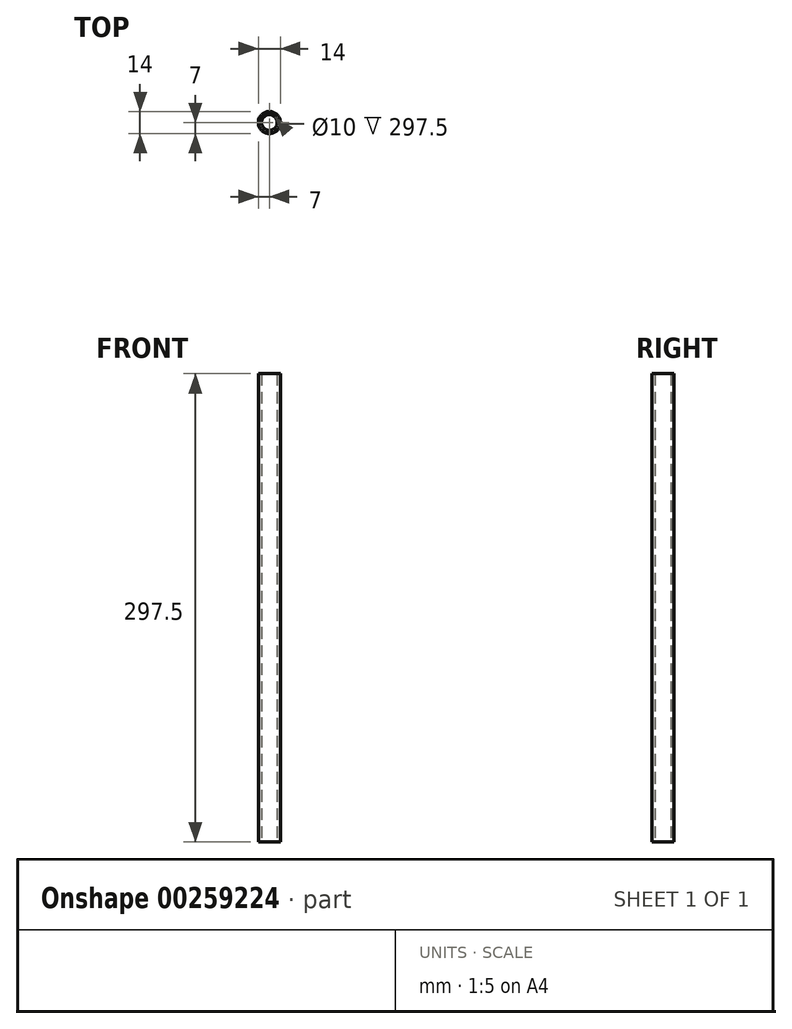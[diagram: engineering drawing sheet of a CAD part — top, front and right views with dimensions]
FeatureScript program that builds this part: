
annotation { "Feature Type Name" : "Feature", "Feature Type Description" : "" }
export const myFeature = defineFeature(function(context is Context, id is Id, definition is map)
    precondition{}
    {
        {
            var Q0;
            Q0=qCreatedBy(makeId("Top.planeOp"),FACE);
            var sketch = newSketch(context, id + "F0", { "sketchPlane" : qUnion([Q0])});
            skCircle(sketch, "E0", {"center": v(0, 0) * mm, "radius": 5 * mm});
            skCircle(sketch, "E1", {"center": v(0, 0) * mm, "radius": 7 * mm});
            skSolve(sketch);
        }
        {
            var Q0;
            Q0=qSketchRegion(id+"F0",true);
            extrude(context, id + "F1", {"entities" : qUnion([Q0]), "depth" : 297.5 * mm});
        }
    });
